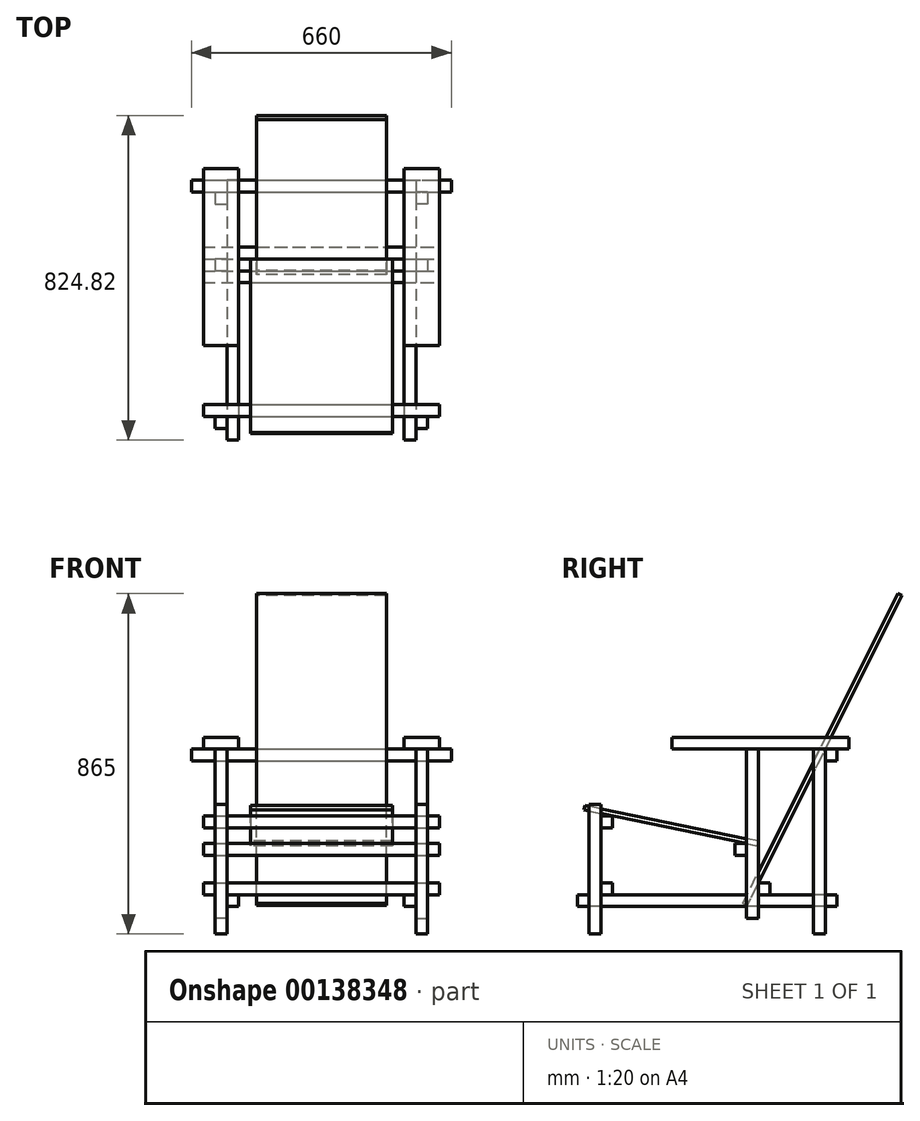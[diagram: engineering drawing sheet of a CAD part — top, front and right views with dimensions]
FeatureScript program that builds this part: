
annotation { "Feature Type Name" : "Feature", "Feature Type Description" : "" }
export const myFeature = defineFeature(function(context is Context, id is Id, definition is map)
    precondition{}
    {
        {
            assignVariable(context, id + "F0", {"name" : "scale", "anyValue" : 1});
        }
        {
            assignVariable(context, id + "F1", {"name" : "baseLength", "anyValue" : 30 * getVariable(context, 'scale')});
        }
        {
            var Q0;
            Q0=qCreatedBy(makeId("Top.planeOp"),FACE);
            var sketch = newSketch(context, id + "F2", { "sketchPlane" : qUnion([Q0])});
            skLineSegment(sketch, "E0.bottom", {"start": v(270, -300) * mm, "end": v(-270, -300) * mm, "construction": true});
            skLineSegment(sketch, "E0.top", {"start": v(270, 300) * mm, "end": v(-270, 300) * mm, "construction": true});
            skLineSegment(sketch, "E0.left", {"start": v(270, -300) * mm, "end": v(270, 300) * mm, "construction": true});
            skLineSegment(sketch, "E0.right", {"start": v(-270, -300) * mm, "end": v(-270, 300) * mm, "construction": true});
            skPoint(sketch, "E0.middle", {"position": v(0, 0) * mm});
            skLineSegment(sketch, "E1", {"start": v(0, 300) * mm, "end": v(0, -300) * mm, "construction": true});
            skLineSegment(sketch, "E2", {"start": v(-270, 0) * mm, "end": v(270, 0) * mm, "construction": true});
            skLineSegment(sketch, "E3.bottom", {"start": v(-270, 300) * mm, "end": v(-240, 300) * mm});
            skLineSegment(sketch, "E3.top", {"start": v(-270, 270) * mm, "end": v(-240, 270) * mm});
            skLineSegment(sketch, "E3.left", {"start": v(-270, 300) * mm, "end": v(-270, 270) * mm});
            skLineSegment(sketch, "E3.right", {"start": v(-240, 300) * mm, "end": v(-240, 270) * mm});
            skLineSegment(sketch, "E4.MirrorCS", {"start": v(270, 270) * mm, "end": v(240, 270) * mm});
            skLineSegment(sketch, "E5.MirrorCS", {"start": v(240, 300) * mm, "end": v(240, 270) * mm});
            skLineSegment(sketch, "E6.MirrorCS", {"start": v(270, 300) * mm, "end": v(240, 300) * mm});
            skLineSegment(sketch, "E7.MirrorCS", {"start": v(270, 300) * mm, "end": v(270, 270) * mm});
            skLineSegment(sketch, "E8.MirrorCS", {"start": v(-270, -270) * mm, "end": v(-240, -270) * mm});
            skLineSegment(sketch, "E9.MirrorCS", {"start": v(-240, -300) * mm, "end": v(-240, -270) * mm});
            skLineSegment(sketch, "E10.MirrorCS", {"start": v(270, -270) * mm, "end": v(240, -270) * mm});
            skLineSegment(sketch, "E11.MirrorCS", {"start": v(240, -300) * mm, "end": v(240, -270) * mm});
            skLineSegment(sketch, "E12.MirrorCS", {"start": v(270, 300) * mm, "end": v(270, -300) * mm, "construction": true});
            skLineSegment(sketch, "E13.MirrorCS", {"start": v(270, -300) * mm, "end": v(270, -270) * mm});
            skLineSegment(sketch, "E14.MirrorCS", {"start": v(270, -300) * mm, "end": v(240, -300) * mm});
            skLineSegment(sketch, "E15.MirrorCS", {"start": v(-270, -300) * mm, "end": v(-240, -300) * mm});
            skLineSegment(sketch, "E16.MirrorCS", {"start": v(-270, -300) * mm, "end": v(-270, -270) * mm});
            skSolve(sketch);
        }
        {
            var Q0;
            Q0=makeQuery(id+"F2.imprint","IMPRINT",FACE,{"disambiguationData":[TD([[makeQuery(id+"F2.imprint","IMPRINT",EDGE,{"derivedFrom":sQuery(id+"F2.wireOp",EDGE,"E10.MirrorCS")}),1.0]])]});
            var Q1;
            Q1=makeQuery(id+"F2.imprint","IMPRINT",FACE,{"disambiguationData":[TD([[makeQuery(id+"F2.imprint","IMPRINT",EDGE,{"derivedFrom":sQuery(id+"F2.wireOp",EDGE,"E8.MirrorCS")}),-1.0]])]});
            extrude(context, id + "F3", {"entities" : qUnion([Q0, Q1]), "depth" : 330 * getVariable(context, 'scale') * mm});
        }
        {
            var Q0;
            Q0=makeQuery(id+"F2.imprint","IMPRINT",FACE,{"disambiguationData":[TD([[makeQuery(id+"F2.imprint","IMPRINT",EDGE,{"derivedFrom":sQuery(id+"F2.wireOp",EDGE,"E3.bottom")}),-1.0]])]});
            var Q1;
            Q1=makeQuery(id+"F2.imprint","IMPRINT",FACE,{"disambiguationData":[TD([[makeQuery(id+"F2.imprint","IMPRINT",EDGE,{"derivedFrom":sQuery(id+"F2.wireOp",EDGE,"E4.MirrorCS")}),-1.0]])]});
            extrude(context, id + "F4", {"entities" : qUnion([Q0, Q1]), "depth" : 470 * getVariable(context, 'scale') * mm});
        }
        {
            var Q0;
            Q0=qCreatedBy(makeId("Top.planeOp"),FACE);
            cPlane(context, id + "F5", {"entities" : qUnion([Q0]), "cplaneType" : CPlaneType.OFFSET, "offset" : (70 * getVariable(context, 'scale')) * mm, "width" : 150 * mm, "height" : 150 * mm});
        }
        {
            var Q0;
            Q0=qCreatedBy(id+"F5.planeOp",FACE);
            var sketch = newSketch(context, id + "F6", { "sketchPlane" : qUnion([Q0])});
            skLineSegment(sketch, "E17.bottom", {"start": v(-210, 330) * mm, "end": v(-240, 330) * mm});
            skLineSegment(sketch, "E17.top", {"start": v(-210, -330) * mm, "end": v(-240, -330) * mm});
            skLineSegment(sketch, "E17.left", {"start": v(-210, 330) * mm, "end": v(-210, -330) * mm});
            skLineSegment(sketch, "E17.right", {"start": v(-240, 330) * mm, "end": v(-240, -330) * mm});
            skLineSegment(sketch, "E18.MirrorCS", {"start": v(240, 330) * mm, "end": v(240, -330) * mm});
            skLineSegment(sketch, "E19.MirrorCS", {"start": v(210, 330) * mm, "end": v(240, 330) * mm});
            skLineSegment(sketch, "E20.MirrorCS", {"start": v(210, 330) * mm, "end": v(210, -330) * mm});
            skLineSegment(sketch, "E21.MirrorCS", {"start": v(210, -330) * mm, "end": v(240, -330) * mm});
            skLineSegment(sketch, "E22.bottom", {"start": v(-240, 130) * mm, "end": v(-270, 130) * mm});
            skLineSegment(sketch, "E22.top", {"start": v(-240, 100) * mm, "end": v(-270, 100) * mm});
            skLineSegment(sketch, "E22.left", {"start": v(-240, 130) * mm, "end": v(-240, 100) * mm});
            skLineSegment(sketch, "E22.right", {"start": v(-270, 130) * mm, "end": v(-270, 100) * mm});
            skLineSegment(sketch, "E23.MirrorCS", {"start": v(240, 100) * mm, "end": v(270, 100) * mm});
            skLineSegment(sketch, "E24.MirrorCS", {"start": v(270, 130) * mm, "end": v(270, 100) * mm});
            skLineSegment(sketch, "E25.MirrorCS", {"start": v(240, 130) * mm, "end": v(270, 130) * mm});
            skSolve(sketch);
        }
        {
            var Q0;
            Q0=makeQuery(id+"F6.imprint","IMPRINT",FACE,{"disambiguationData":[TD([[makeQuery(id+"F6.imprint","IMPRINT",EDGE,{"derivedFrom":sQuery(id+"F6.wireOp",EDGE,"E17.bottom")}),1.0]])]});
            var Q1;
            Q1=makeQuery(id+"F6.imprint","IMPRINT",FACE,{"disambiguationData":[TD([[makeQuery(id+"F6.imprint","IMPRINT",EDGE,{"derivedFrom":sQuery(id+"F6.wireOp",EDGE,"E18.MirrorCS")}),-1.0]])]});
            extrude(context, id + "F7", {"entities" : qUnion([Q0, Q1]), "depth" : getVariable(context, 'baseLength') * mm});
        }
        {
            var Q0;
            Q0=makeQuery(id+"F6.imprint","IMPRINT",FACE,{"disambiguationData":[TD([[makeQuery(id+"F6.imprint","IMPRINT",EDGE,{"derivedFrom":sQuery(id+"F6.wireOp",EDGE,"E22.bottom")}),1.0]])]});
            var Q1;
            {var subQ0=sQuery(id+"F6.wireOp",EDGE,"E23.MirrorCS");Q1=makeQuery(id+"F6.imprint","IMPRINT",FACE,{"disambiguationData":[TD([[makeQuery(id+"F6.imprint","IMPRINT",EDGE,{"derivedFrom":subQ0}),1.0]])]});}
            var Q2;
            Q2=makeQuery(id+"F4.opExtrude","CAP_FACE",FACE,{"disambiguationData":[OSD([sQuery(id+"F2.wireOp",EDGE,"E3.bottom"),sQuery(id+"F2.wireOp",EDGE,"E3.top"),sQuery(id+"F2.wireOp",EDGE,"E3.left"),sQuery(id+"F2.wireOp",EDGE,"E3.right")])],"isStart":false});
            extrude(context, id + "F8", {"entities" : qUnion([Q0, Q1]), "endBound" : BoundingType.UP_TO_SURFACE, "endBoundEntityFace" : qUnion([Q2]), "depth" : 25 * mm, "hasSecondDirection" : true, "secondDirectionOppositeDirection" : true, "secondDirectionDepth" : getVariable(context, 'baseLength') * mm});
        }
        {
            var Q0;
            Q0=makeQuery(id+"F4.opExtrude","CAP_FACE",FACE,{"disambiguationData":[OSD([sQuery(id+"F2.wireOp",EDGE,"E3.bottom"),sQuery(id+"F2.wireOp",EDGE,"E3.top"),sQuery(id+"F2.wireOp",EDGE,"E3.left"),sQuery(id+"F2.wireOp",EDGE,"E3.right")])],"isStart":false});
            var sketch = newSketch(context, id + "F9", { "sketchPlane" : qUnion([Q0])});
            skLineSegment(sketch, "E26.bottom", {"start": v(-210, 360) * mm, "end": v(-300, 360) * mm});
            skLineSegment(sketch, "E26.top", {"start": v(-210, -90) * mm, "end": v(-300, -90) * mm});
            skLineSegment(sketch, "E26.left", {"start": v(-210, 360) * mm, "end": v(-210, -90) * mm});
            skLineSegment(sketch, "E26.right", {"start": v(-300, 360) * mm, "end": v(-300, -90) * mm});
            skLineSegment(sketch, "E27", {"start": v(-270, 300) * mm, "end": v(-300, 300) * mm, "construction": true});
            skLineSegment(sketch, "E28", {"start": v(-270, 300) * mm, "end": v(-270, 360) * mm, "construction": true});
            skLineSegment(sketch, "E29", {"start": v(-240, 270) * mm, "end": v(-300, 270) * mm, "construction": true});
            skLineSegment(sketch, "E30.MirrorCS", {"start": v(210, 360) * mm, "end": v(300, 360) * mm});
            skLineSegment(sketch, "E31.MirrorCS", {"start": v(300, 360) * mm, "end": v(300, -90) * mm});
            skLineSegment(sketch, "E32.MirrorCS", {"start": v(210, -90) * mm, "end": v(300, -90) * mm});
            skLineSegment(sketch, "E33.MirrorCS", {"start": v(210, 360) * mm, "end": v(210, -90) * mm});
            skSolve(sketch);
        }
        {
            var Q0;
            Q0=makeQuery(id+"F9.imprint","IMPRINT",FACE,{"disambiguationData":[TD([[makeQuery(id+"F9.imprint","IMPRINT",EDGE,{"derivedFrom":sQuery(id+"F9.wireOp",EDGE,"E26.bottom")}),1.0]])]});
            var Q1;
            Q1=makeQuery(id+"F9.imprint","IMPRINT",FACE,{"disambiguationData":[TD([[makeQuery(id+"F9.imprint","IMPRINT",EDGE,{"derivedFrom":sQuery(id+"F9.wireOp",EDGE,"E30.MirrorCS")}),-1.0]])]});
            var Q2;
            Q2=makeQuery(id+"F9.imprint","IMPRINT",FACE,{"disambiguationData":[TD([[makeQuery(id+"F9.imprint","IMPRINT",EDGE,{"derivedFrom":makeQuery(id+"F4.opExtrude","CAP_EDGE",EDGE,{"disambiguationData":[OSD([sQuery(id+"F2.wireOp",EDGE,"E3.bottom")])],"isStart":false})}),-1.0]])]});
            extrude(context, id + "F10", {"entities" : qUnion([Q0, Q1, Q2]), "depth" : getVariable(context, 'baseLength') * mm});
        }
        {
            var Q0;
            Q0=makeQuery(id+"F4.opExtrude","SWEPT_FACE",FACE,{"disambiguationData":[OSD([sQuery(id+"F2.wireOp",EDGE,"E3.left")])]});
            var sketch = newSketch(context, id + "F11", { "sketchPlane" : qUnion([Q0])});
            skLineSegment(sketch, "E34.bottom", {"start": v(-160, 130) * mm, "end": v(-130, 130) * mm});
            skLineSegment(sketch, "E34.top", {"start": v(-160, 100) * mm, "end": v(-130, 100) * mm});
            skLineSegment(sketch, "E34.left", {"start": v(-160, 130) * mm, "end": v(-160, 100) * mm});
            skLineSegment(sketch, "E34.right", {"start": v(-130, 130) * mm, "end": v(-130, 100) * mm});
            skLineSegment(sketch, "E35.bottom", {"start": v(240, 130) * mm, "end": v(270, 130) * mm});
            skLineSegment(sketch, "E35.top", {"start": v(240, 100) * mm, "end": v(270, 100) * mm});
            skLineSegment(sketch, "E35.left", {"start": v(240, 130) * mm, "end": v(240, 100) * mm});
            skLineSegment(sketch, "E35.right", {"start": v(270, 130) * mm, "end": v(270, 100) * mm});
            skLineSegment(sketch, "E36.bottom", {"start": v(240, 300) * mm, "end": v(270, 300) * mm});
            skLineSegment(sketch, "E36.top", {"start": v(240, 270) * mm, "end": v(270, 270) * mm});
            skLineSegment(sketch, "E36.left", {"start": v(240, 300) * mm, "end": v(240, 270) * mm});
            skLineSegment(sketch, "E36.right", {"start": v(270, 300) * mm, "end": v(270, 270) * mm});
            skLineSegment(sketch, "E37.bottom", {"start": v(-100, 230) * mm, "end": v(-70, 230) * mm});
            skLineSegment(sketch, "E37.top", {"start": v(-100, 200) * mm, "end": v(-70, 200) * mm});
            skLineSegment(sketch, "E37.left", {"start": v(-100, 230) * mm, "end": v(-100, 200) * mm});
            skLineSegment(sketch, "E37.right", {"start": v(-70, 230) * mm, "end": v(-70, 200) * mm});
            skSolve(sketch);
        }
        {
            var Q0;
            Q0=makeQuery(id+"F11.imprint","IMPRINT",FACE,{"disambiguationData":[TD([[makeQuery(id+"F11.imprint","IMPRINT",EDGE,{"derivedFrom":sQuery(id+"F11.wireOp",EDGE,"E34.bottom")}),-1.0]])]});
            var Q1;
            Q1=makeQuery(id+"F11.imprint","IMPRINT",FACE,{"disambiguationData":[TD([[makeQuery(id+"F11.imprint","IMPRINT",EDGE,{"derivedFrom":sQuery(id+"F11.wireOp",EDGE,"E35.bottom")}),-1.0]])]});
            var Q2;
            Q2=makeQuery(id+"F11.imprint","IMPRINT",FACE,{"disambiguationData":[TD([[makeQuery(id+"F11.imprint","IMPRINT",EDGE,{"derivedFrom":sQuery(id+"F11.wireOp",EDGE,"E37.bottom")}),-1.0]])]});
            var Q3;
            Q3=makeQuery(id+"F11.imprint","IMPRINT",FACE,{"disambiguationData":[TD([[makeQuery(id+"F11.imprint","IMPRINT",EDGE,{"derivedFrom":sQuery(id+"F11.wireOp",EDGE,"E36.bottom")}),-1.0]])]});
            var Q4;
            Q4=makeQuery(id+"F10.opExtrude","SWEPT_FACE",FACE,{"disambiguationData":[OSD([sQuery(id+"F9.wireOp",EDGE,"E26.right")])]});
            var Q5;
            Q5=makeQuery(id+"F10.opExtrude","SWEPT_FACE",FACE,{"disambiguationData":[OSD([sQuery(id+"F9.wireOp",EDGE,"E31.MirrorCS")])]});
            extrude(context, id + "F12", {"entities" : qUnion([Q0, Q1, Q2, Q3]), "endBound" : BoundingType.UP_TO_SURFACE, "endBoundEntityFace" : qUnion([Q4]), "depth" : 25 * mm, "hasSecondDirection" : true, "secondDirectionBound" : BoundingType.UP_TO_SURFACE, "secondDirectionOppositeDirection" : true, "secondDirectionBoundEntityFace" : qUnion([Q5]), "secondDirectionDepth" : 25 * mm});
        }
        {
            var Q0;
            Q0=makeQuery(id+"F10.opExtrude","CAP_FACE",FACE,{"disambiguationData":[OSD([sQuery(id+"F9.wireOp",EDGE,"E30.MirrorCS"),sQuery(id+"F9.wireOp",EDGE,"E31.MirrorCS"),sQuery(id+"F9.wireOp",EDGE,"E32.MirrorCS"),sQuery(id+"F9.wireOp",EDGE,"E33.MirrorCS")])],"isStart":true});
            var sketch = newSketch(context, id + "F13", { "sketchPlane" : qUnion([Q0])});
            skLineSegment(sketch, "E38.bottom", {"start": v(-330, -330) * mm, "end": v(330, -330) * mm});
            skLineSegment(sketch, "E38.top", {"start": v(-330, -300) * mm, "end": v(330, -300) * mm});
            skLineSegment(sketch, "E38.left", {"start": v(-330, -330) * mm, "end": v(-330, -300) * mm});
            skLineSegment(sketch, "E38.right", {"start": v(330, -330) * mm, "end": v(330, -300) * mm});
            skSolve(sketch);
        }
        {
            var Q0;
            {var subQ0=sQuery(id+"F13.wireOp",EDGE,"E38.left");Q0=makeQuery(id+"F13.imprint","IMPRINT",FACE,{"disambiguationData":[TD([[makeQuery(id+"F13.imprint","IMPRINT",EDGE,{"derivedFrom":subQ0}),-1.0]])]});}
            var Q1;
            {var subQ0=sQuery(id+"F13.wireOp",EDGE,"E38.right");Q1=makeQuery(id+"F13.imprint","IMPRINT",FACE,{"disambiguationData":[TD([[makeQuery(id+"F13.imprint","IMPRINT",EDGE,{"derivedFrom":subQ0}),1.0]])]});}
            var Q2;
            {var subQ0=sQuery(id+"F13.wireOp",EDGE,"E38.bottom");var subQ1=makeQuery(id+"F10.opExtrude","CAP_EDGE",EDGE,{"disambiguationData":[OSD([sQuery(id+"F9.wireOp",EDGE,"E33.MirrorCS")])],"isStart":true});var subQ2=makeQuery(id+"F13.imprint","INTERSECT",VERTEX,{"derivedFrom":[subQ1,subQ0]});Q2=makeQuery(id+"F13.imprint","IMPRINT",FACE,{"disambiguationData":[TD([[makeQuery(id+"F13.imprint","IMPRINT",EDGE,{"disambiguationData":[TD([[subQ2,-1.0]])],"derivedFrom":subQ0}),1.0]])]});}
            extrude(context, id + "F14", {"entities" : qUnion([Q0, Q1, Q2]), "depth" : getVariable(context, 'baseLength') * mm});
        }
        {
            var Q0;
            Q0=qCreatedBy(makeId("Right.planeOp"),FACE);
            var sketch = newSketch(context, id + "F15", { "sketchPlane" : qUnion([Q0])});
            skLineSegment(sketch, "E39", {"start": v(-313, 315.03) * mm, "end": v(127.76, 224.29) * mm});
            skLineSegment(sketch, "E40", {"start": v(127.76, 224.29) * mm, "end": v(130.18, 236.04) * mm});
            skLineSegment(sketch, "E41", {"start": v(130.18, 236.04) * mm, "end": v(-310.58, 326.78) * mm});
            skLineSegment(sketch, "E42", {"start": v(-310.58, 326.78) * mm, "end": v(-313, 315.03) * mm});
            skLineSegment(sketch, "E43", {"start": v(494.82, 859.63) * mm, "end": v(101.27, 72.54) * mm});
            skLineSegment(sketch, "E44", {"start": v(101.27, 72.54) * mm, "end": v(90.54, 77.9) * mm});
            skLineSegment(sketch, "E45", {"start": v(90.54, 77.9) * mm, "end": v(484.08, 865) * mm});
            skLineSegment(sketch, "E46", {"start": v(484.08, 865) * mm, "end": v(494.82, 859.63) * mm});
            skLineSegment(sketch, "E47.0", {"start": v(130, 40) * mm, "end": v(100, 40) * mm, "construction": true});
            skPoint(sketch, "E48.0", {"position": v(100, 230) * mm});
            skPoint(sketch, "E48.1", {"position": v(-240, 300) * mm});
            skSolve(sketch);
        }
        {
            var Q0;
            Q0=makeQuery(id+"F15.imprint","IMPRINT",FACE,{"disambiguationData":[TD([[makeQuery(id+"F15.imprint","IMPRINT",EDGE,{"derivedFrom":sQuery(id+"F15.wireOp",EDGE,"E39")}),1.0]])]});
            extrude(context, id + "F16", {"entities" : qUnion([Q0]), "depth" : 360 * getVariable(context, 'scale') * mm, "symmetric" : true});
        }
        {
            var Q0;
            Q0=makeQuery(id+"F15.imprint","IMPRINT",FACE,{"disambiguationData":[TD([[makeQuery(id+"F15.imprint","IMPRINT",EDGE,{"derivedFrom":sQuery(id+"F15.wireOp",EDGE,"E43")}),-1.0]])]});
            extrude(context, id + "F17", {"entities" : qUnion([Q0]), "depth" : 330 * getVariable(context, 'scale') * mm, "symmetric" : true});
        }
    });
